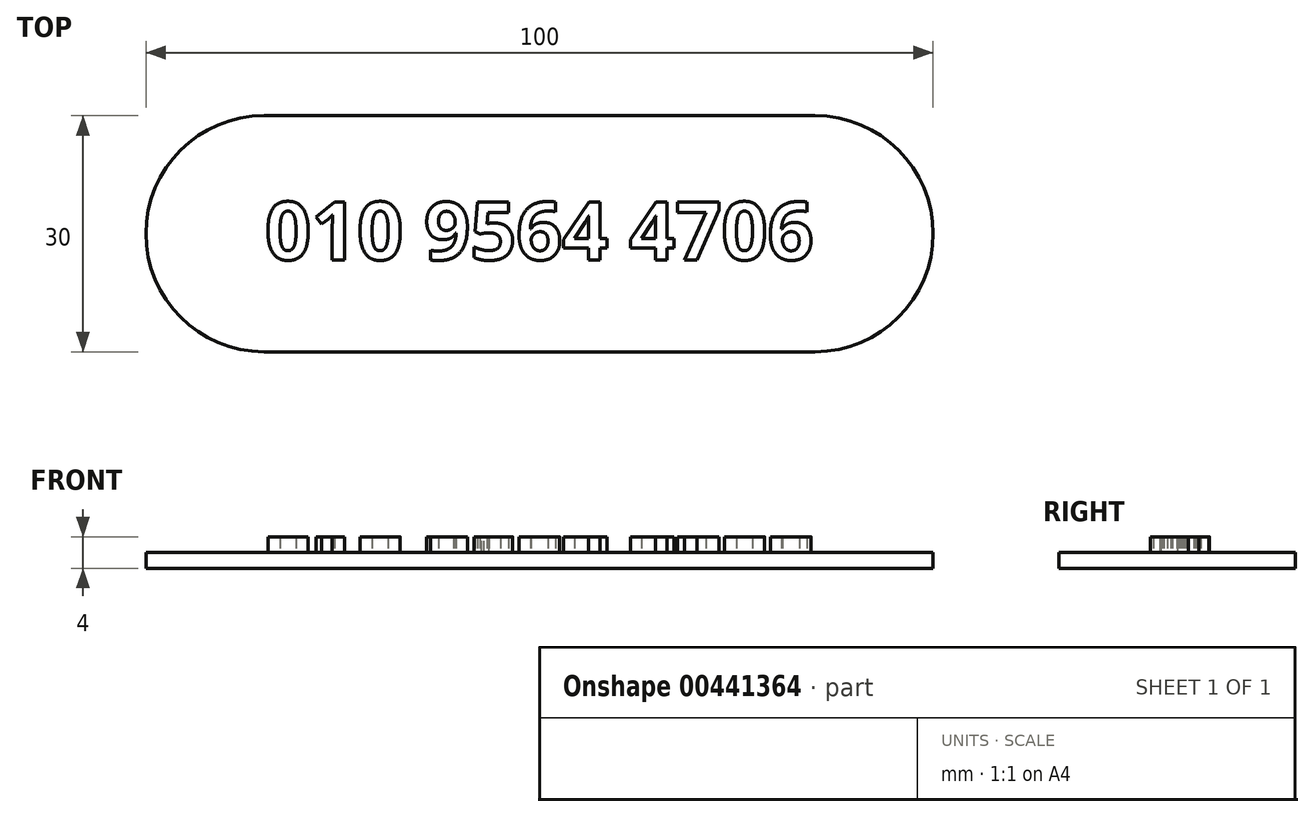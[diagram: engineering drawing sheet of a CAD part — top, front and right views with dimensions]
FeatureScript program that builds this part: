
annotation { "Feature Type Name" : "Feature", "Feature Type Description" : "" }
export const myFeature = defineFeature(function(context is Context, id is Id, definition is map)
    precondition{}
    {
        {
            var Q0;
            Q0=qCreatedBy(makeId("Top.planeOp"),FACE);
            var sketch = newSketch(context, id + "F0", { "sketchPlane" : qUnion([Q0])});
            skLineSegment(sketch, "E0.bottom", {"start": v(35, -15) * mm, "end": v(-35, -15) * mm});
            skLineSegment(sketch, "E0.top", {"start": v(35, 15) * mm, "end": v(-35, 15) * mm});
            skLineSegment(sketch, "E0.left", {"start": v(35, -15) * mm, "end": v(35, 15) * mm});
            skLineSegment(sketch, "E0.right", {"start": v(-35, -15) * mm, "end": v(-35, 15) * mm});
            skPoint(sketch, "E0.middle", {"position": v(0, 0) * mm});
            skCircle(sketch, "E1", {"center": v(-35, 0) * mm, "radius": 15 * mm});
            skCircle(sketch, "E2", {"center": v(35, 0) * mm, "radius": 15 * mm});
            skSolve(sketch);
        }
        {
            var Q0;
            Q0=qSketchRegion(id+"F0",true);
            extrude(context, id + "F1", {"entities" : qUnion([Q0]), "oppositeDirection" : true, "depth" : 2 * mm});
        }
        {
            var Q0;
            Q0=makeQuery(id+"F1.opExtrude","CAP_FACE",FACE,{"disambiguationData":[OSD([sQuery(id+"F0.wireOp",EDGE,"E0.bottom"),sQuery(id+"F0.wireOp",EDGE,"E0.top"),sQuery(id+"F0.wireOp",EDGE,"E1"),sQuery(id+"F0.wireOp",EDGE,"E2")])],"isStart":true});
            var sketch = newSketch(context, id + "F2", { "sketchPlane" : qUnion([Q0])});
            skText(sketch, "E3", { "text": "010 9564 4706", "fontName": "OpenSans-Bold.ttf"});
            const initialGuessF2  = {"E3": [-0.03487, -0.00331, 1, 0, 0.00738]};
            skSetInitialGuess(sketch, initialGuessF2);
            skSolve(sketch);
        }
        {
            var Q0;
            Q0 = qSketchRegion(id + "F2", true);
            extrude(context, id + "F3", {"entities" : qUnion([Q0]), "operationType" : NewBodyOperationType.ADD, "depth" : 2 * mm});
        }
    });
